# Revit family: IS_Tipo-Z_T4426_BIM_NL
name_source: partatom
category: Plumbing Fixtures
units: mm (PartAtom-declared; Revit-internal decimal feet)

## family parameters
Always vertical = No
Cut with Voids When Loaded = No
OmniClass Number = 23.45.05.14.14
OmniClass Title = Sinks/Lavatories
Part Type = Normal
Room Calculation Point = No
Round Connector Dimension = Use Diameter
Shared = No
Work Plane-Based = No

## types (4) — shared parameters
Accesoires = https://www.idealstandard.nl
Accessories = https://www.idealstandard.nl
Afmetingen = 740 x 469 x 900 mm
AfstandsEenheid = Millimeter
AreaUnits = millimeter
Artikelreferentie = Tipo-Z One Piece Basin & Pedestal, 3 Tap Holes, With Overflow
AssetType = Fixed
Auteur = Ideal Standard
BIMObjectName = IS_IdealStandard_Wall-hungwashbasins_Tipo-Z_T4426
BIMobject category = Wash Basins
BIMobject category code = wash-basins
BIMobject main category = Sanitary
BIMobject main category code = sanitary
Beschrijvinggarantie = Herstellergarantie
BimObjectNaam = IS_IdealStandard_Wall-hungwashbasins_Tipo-Z_T4426
Brand = Ideal Standard
Brand url = https://www.idealstandard.nl
Breedte = 740.00024
ConnectionType = Plumbing
CurrencyUnit = €
CurrentRevision = 1
Date of publishing = 15/10/2021
DurationUnit = Years
DuurEenheid = Jahre
Edition number = 1
Garantieonderdelen = 5
Garantieunits = Jahre
GemaaktOp = 15/10/2021
Help = https://www.idealstandard.nl
Hoogte = 900.000058914433
Hulp = https://www.idealstandard.nl
IFC Classification = Sanitary Terminal
IfcExportAs = IfcSanitaryTerminalType
IfcExportType = WASHHANDBASIN
Installatieinstructies = https://www.idealstandard.nl
Installation instructions = https://www.idealstandard.nl
InstallationInstructions = https://www.idealstandard.nl
Lengte = 470 mm
LinearUnits = millimeter
MaintenanceInformation = https://www.idealstandard.nl
Manufacturer = Ideal Standard
Manufacturer name = Ideal Standard
ManufacturerURL = https://www.idealstandard.nl
Masterformat 2014 Code = 33 47 26.16
Masterformat 2014 Description = Retention Basins
Materiaal = Fine Fire Clay
Material = FineFireClay
Material main = FineFireClay
Merk = Ideal Standard
Montageinstuctie = Selbststehendes Waschbecken
NBS Reference Code = 45-35-70/369
NBS Reference Description = Wall hung wash basins
Name = Wall-hungwashbasins_Tipo-Z_T4426_IdealStandard
NettWeight = 33.4
Nettogewicht = 33.4
NominalDepth = 469 mm
NominalHeight = 900 mm  [stored 2.95276 ft]
NominalLength = 470 mm
NominalWidth = 740 mm  [stored 2.42782 ft]
Normen = Wall-hungwashbasins_Tipo-Z_T4426_IdealStandard
OmniClass Code = 23-39 29 13 21 19
OmniClass Description = Surface Water Retention Basins
Ophangingwastafel = staande wastafel
OppervlakteEenheid = Millimeter
Product Guid = 28f87708-75d3-4fcb-94e8-a73e8b8fc5d0
Product SKU = T4426
Product certification = https://www.idealstandard.nl
Product data url = https://bimobject.com
Product family = Sanitary
Product group = Basin
Product name = Tipo-Z
Product url = https://www.idealstandard.nl
ProductInformation = https://www.idealstandard.nl
Productinformatie = https://www.idealstandard.nl
QR code = http://bimobject.com
Revisie = 1
Shape = Sculpture
Size = 740 x 469 x 900 mm
Space = Internal
SpareParts = https://www.idealstandard.nl
Technical description = https://www.idealstandard.nl
Telefoonnummer = 077 355 08 08
Typeconnectie = installation
Typewastafel = staande wastafel
UNSPSC Code = 301815
URL = https://www.idealstandard.nl
Uniclass 1.4 Code = L7212
Uniclass 1.4 Description = Washbasin
Uniclass 2.0 Code = PR-31-79
Uniclass 2.0 Description = Sinks, Wash Basins And Troughs
Uniclass 2015 Code = Pr_40_20_96_96
Uniclass 2015 Name = Wall-hung washbasins
Uniclass2015Beschrijving = Wall-hung washbasins
Uniclass2015Referentie = Pr_40_20_96_96
Uniclass2015Version = Wall-hung washbasins
Urlproducent = https://www.idealstandard.nl
ValutaEenheid = Euro
Versie = 1
Version = v1.22
VolumeUnits = Liters
Volumeunits = Liter
Vorm = gemeißelt
WRASURL = https://www.wrasapprovals.co.uk
WarrantyDescription = manufacturer warranty
WarrantyDurationParts = 99
WarrantyDurationUnit = Years
WashHandBasinMounting = self standing
WashHandBasinType = Self Standaing Washbasin
Youtube clip = https://www.youtube.com
zero-valued in all types: BrutoGewicht, Diepte, InletConnectionSize, MaterialThickness, Vervangingskosten

## per-type parameters (varying)
| type | Afwerking | Artikelnummer | Artikelomschrijving | BarCode | Color | Description | Eigenschappen | ExpectedLife | Features | Finish | GTIN code | Kleur | MainColor | Model | ModelNumber | ModelReference | Referentie |
| T442601 - Tipo-Z One Piece Basin & Pedestal, 3 Tap Holes, With Overflow - Glossy White | Weiß | T442601 | Tipo-Z Einteiliges Waschbecken & Standfuß mit 3 Hahnlöchern und geschlitztem Überlauf in glänzend weißem Finish | 8014140491309 | White | Tipo-Z Einteiliges Waschbecken & Standfuß mit 3 Hahnlöchern und geschlitztem Überlauf in glänzend weißem Finish | Einteiliges Waschbecken und Sockel mit 3 Hahnlöchern und geschlitztem Überlauf in glänzend weißem Finish | 103 | Einteiliges Waschbecken und Sockel mit 3 Hahnlöchern und geschlitztem Überlauf in glänzend weißem Finish | Weiß | https://8014140491309 | White | Weiß | T442601 | T442601 | T442601 | T442601 |
| T4426V1 - Tipo-Z One Piece Basin & Pedestal, 3 Tap Holes, With Overflow - Silk White | Seide weiß | T4426V1 | Tipo-Z Einteiliges Waschbecken & Sockel mit 3 Hahnlöchern und geschlitztem Überlauf in seidenweißem Finish | 8014140491316 | Silk white | Tipo-Z Einteiliges Waschbecken & Sockel mit 3 Hahnlöchern und geschlitztem Überlauf in seidenweißem Finish | Einteiliges Waschbecken und Sockel mit 3 Hahnlöchern und geschlitztem Überlauf in seidenweißem Finish | 104 | Einteiliges Waschbecken und Sockel mit 3 Hahnlöchern und geschlitztem Überlauf in seidenweißem Finish | Seide weiß | https://8014140491316 | Silk white | Seide weiß | T4426V1 | T4426V1 | T4426V1 | T4426V1 |
| T4426V2 - Tipo-Z One Piece Basin & Pedestal, 3 Tap Holes, With Overflow - Glossy Black | Schwarz glänzend | T4426V2 | Tipo-Z Einteiliges Waschbecken & Sockel mit 3 Hahnlöchern und geschlitztem Überlauf in glänzend schwarzem Finish | 8014140491323 | Gloss Black | Tipo-Z Einteiliges Waschbecken & Sockel mit 3 Hahnlöchern und geschlitztem Überlauf in glänzend schwarzem Finish | Einteiliges Waschbecken und Sockel mit 3 Hahnlöchern und geschlitztem Überlauf in glänzend schwarzem Finish | 105 | Einteiliges Waschbecken und Sockel mit 3 Hahnlöchern und geschlitztem Überlauf in glänzend schwarzem Finish | Schwarz glänzend | https://8014140491323 | Gloss Black | Schwarz glänzend | T4426V2 | T4426V2 | T4426V2 | T4426V2 |
| T4426V3 - Tipo-Z One Piece Basin & Pedestal, 3 Tap Holes, With Overflow - Silk Black | Seide Schwarz | T4426V3 | Tipo-Z Einteiliges Waschbecken & Sockel mit 3 Hahnlöchern und geschlitztem Überlauf in seidenschwarzer Oberfläche | 8014140491330 | Silk Black | Tipo-Z Einteiliges Waschbecken & Sockel mit 3 Hahnlöchern und geschlitztem Überlauf in seidenschwarzer Oberfläche | Einteiliges Waschbecken und Sockel mit 3 Hahnlöchern und geschlitztem Überlauf in seidenschwarzem Finish | 106 | Einteiliges Waschbecken und Sockel mit 3 Hahnlöchern und geschlitztem Überlauf in seidenschwarzem Finish | Seide Schwarz | https://8014140491330 | Silk Black | Seide Schwarz | T4426V3 | T4426V3 | T4426V3 | T4426V3 |

note: [stored X ft] marks values corroborated as IEEE doubles in the binary element streams (Revit-internal decimal feet)

## geometry (parser evidence)
native form markers: Sweep x4
no freeform markers — native parametric forms only
